# Revit family: Furniture-Mirror-KALLISTA-One-P74053
name_source: partatom
category: Specialty Equipment
units: mm (PartAtom-declared; Revit-internal decimal feet)

## family parameters
Cut with Voids When Loaded = No
Host = Face
Maintain Annotation Orientation = No
OmniClass Number = 23.31.25.00
OmniClass Title = Toilet and Bath Specialties
Part Type = Normal
Room Calculation Point = No
Round Connector Dimension = Use Diameter
Shared = No

## types (4) — shared parameters
ADA Compliant = No
Assembly Code = E20
Date Modified = 06/22/2025
Default Elevation = 48"
Height = 33"
Length = 19 1/2"
Manufacturer = Kallista Co.
Master Format 2014 = 06 41 93
Master Format 2014 Name = Cabinet and Drawer Hardware
Material = Premium Metal Construction
Model = Mirror
Product Documentation Link = https://techcomm.kohler.com
Product Name = One
URL = https://www.kallista.com
WaterSense Certified = No
Width = 2"

## per-type parameters (varying)
| type | Description | Finish | Product Page URL | Type |
| BL-Matte Black | P74053-00-BL | Kallista-Metal-BL-Matte_Black | https://www.kallista.com | 1 |
| BN-Brushed Nickel | P74053-00-BN | Kallista-Metal-BN-Brushed_Nickel |  | 2 |
| BV-Brushed Bronze | P74053-00-BV | Kallista-Metal-BV-Brushed_Bronze |  | 3 |
| ULB-Unlaquered Brass | P74053-00-ULB | Kallista-Metal-ULB-Unlaquered_Brass |  | 4 |

## geometry (parser evidence)
native form markers: Sweep x6
no freeform markers — native parametric forms only
